# Revit family: MT-HB_BIFOLD DOOR_XX
name_source: partatom
category: Doors
revit_build: Autodesk Revit 2017 (Build: 20160225_1515(x64)
units: mm (PartAtom-declared; Revit-internal decimal feet)

## family parameters
Always vertical = Yes
Cut with Voids When Loaded = No
Host = Wall
OmniClass Number = 23.30.20.00
OmniClass Title = Windows
Room Calculation Point = No
Shared = No

## types (2) — shared parameters
101.6mm FRAME THICKNESS = Yes
150mm FRAME THICKNESS = No
1L1R = Yes
2L/2R = No
AIR POCKET = 8 mm  [stored 0.0262467 ft]
ANZRC COMPLIANT = YES
Analytic Construction = <None>
BOT PANEL POSITION = 35 mm
DETAIL_DEPTH SILL = 102 mm
DOUBLE GLAZED = Yes
DOUBLE GLAZED THICKNESS = 18 mm  [stored 0.0590551 ft]
FRAME MATERIAL = <By Category>
FRAME THICKNESS = 102 mm
GLAZED MATERIAL = Glass
Height = 2100 mm  [stored 6.88976 ft]
MAX HEIGHT = 3000 mm  [stored 9.84252 ft]
MAX PANEL HEIGHT = 3000 mm  [stored 9.84252 ft]
MAX PANEL WIDTH = 1000 mm  [stored 3.28084 ft]
MAX WIDTH = 2000 mm  [stored 6.56168 ft]
Manufacturer = ALSPEC
Model = HAWKESBURY TOP HUNG COMMERCIAL MULTI-FOLD DOOR
OFFSET = 10 mm  [stored 0.0328084 ft]
OVERALL FRAME HEIGHT = 2100 mm  [stored 6.88976 ft]
OVERALL FRAME WIDTH = 2000 mm  [stored 6.56168 ft]
PANEL HEIGHT = 1982 mm
PANEL WIDTH = 948 mm
Rough Height = 2100 mm  [stored 6.88976 ft]
Rough Width = 2000 mm  [stored 6.56168 ft]
SINGLE GLAZED THICKNESS = 5 mm  [stored 0.0164042 ft]
TOP PANEL POSITION = 1966 mm
URL = WWW.ALSPEC.COM.AU
VERSION = 2.1
WARNING = No
Wall Closure = By host
Width = 2000 mm  [stored 6.56168 ft]
YEAR = 2019
zero-valued in all types: Default Sill Height, TOLERANCE

## type names (no varying parameters)
- 2L/2R
- 1L1R

note: [stored X ft] marks values corroborated as IEEE doubles in the binary element streams (Revit-internal decimal feet)

## geometry (parser evidence)
native form markers: Sweep x34
no freeform markers — native parametric forms only
